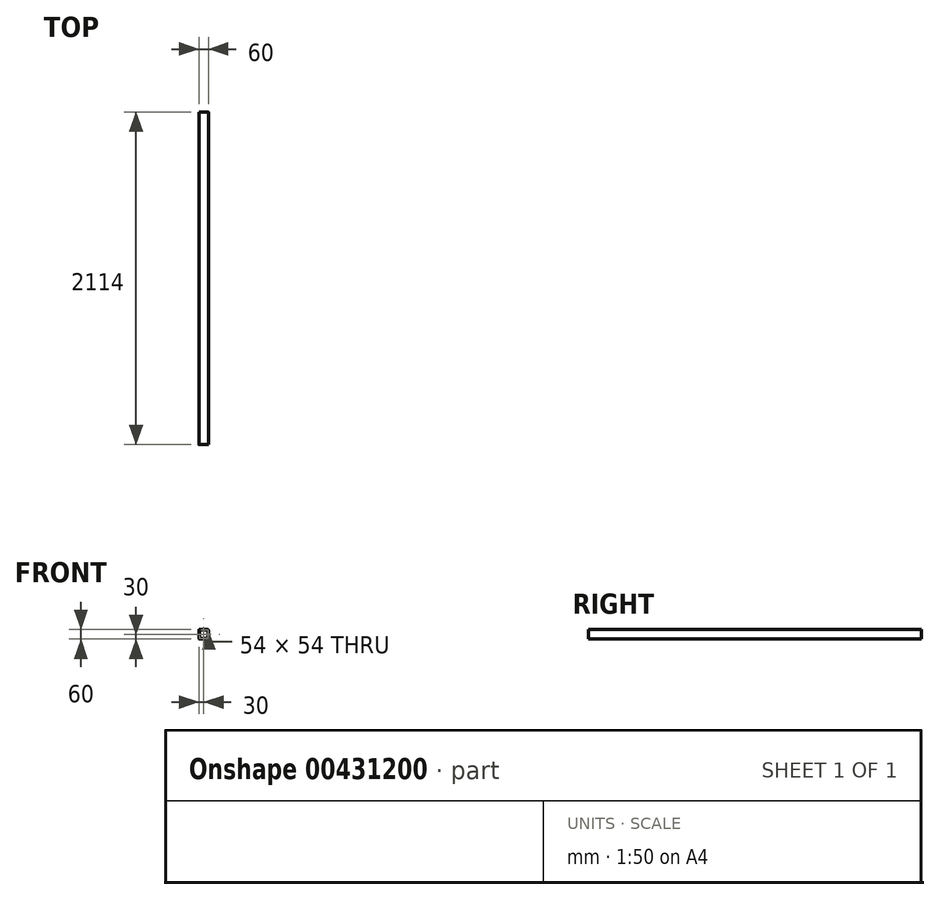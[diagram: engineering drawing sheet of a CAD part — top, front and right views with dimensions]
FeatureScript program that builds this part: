
annotation { "Feature Type Name" : "Feature", "Feature Type Description" : "" }
export const myFeature = defineFeature(function(context is Context, id is Id, definition is map)
    precondition{}
    {
        {
            var Q0;
            Q0=qCreatedBy(makeId("Front.planeOp"),FACE);
            var sketch = newSketch(context, id + "F0", { "sketchPlane" : qUnion([Q0])});
            skLineSegment(sketch, "E0.bottom", {"start": v(27, -30) * mm, "end": v(-27, -30) * mm});
            skLineSegment(sketch, "E0.top", {"start": v(27, 30) * mm, "end": v(-27, 30) * mm});
            skLineSegment(sketch, "E0.left", {"start": v(30, -27) * mm, "end": v(30, 27) * mm});
            skLineSegment(sketch, "E0.right", {"start": v(-30, -27) * mm, "end": v(-30, 27) * mm});
            skPoint(sketch, "E0.middle", {"position": v(0, 0) * mm});
            skLineSegment(sketch, "E1.bottom", {"start": v(27, -27) * mm, "end": v(-27, -27) * mm});
            skLineSegment(sketch, "E1.top", {"start": v(27, 27) * mm, "end": v(-27, 27) * mm});
            skLineSegment(sketch, "E1.left", {"start": v(27, -27) * mm, "end": v(27, 27) * mm});
            skLineSegment(sketch, "E1.right", {"start": v(-27, -27) * mm, "end": v(-27, 27) * mm});
            skPoint(sketch, "E2.visualSharp", {"position": v(-30, 30) * mm});
            skArc(sketch, "E2.filletArc", {"start": v(-27, 30) * mm, "mid": v(-29.12, 29.12) * mm, "end": v(-30, 27) * mm});
            skPoint(sketch, "E3.visualSharp", {"position": v(30, 30) * mm});
            skArc(sketch, "E3.filletArc", {"start": v(30, 27) * mm, "mid": v(29.12, 29.12) * mm, "end": v(27, 30) * mm});
            skPoint(sketch, "E4.visualSharp", {"position": v(30, -30) * mm});
            skArc(sketch, "E4.filletArc", {"start": v(27, -30) * mm, "mid": v(29.12, -29.12) * mm, "end": v(30, -27) * mm});
            skPoint(sketch, "E5.visualSharp", {"position": v(-30, -30) * mm});
            skArc(sketch, "E5.filletArc", {"start": v(-30, -27) * mm, "mid": v(-29.12, -29.12) * mm, "end": v(-27, -30) * mm});
            skSolve(sketch);
        }
        {
            var Q0;
            Q0=qSketchRegion(id+"F0",true);
            extrude(context, id + "F1", {"entities" : qUnion([Q0]), "depth" : 2114 * mm});
        }
    });
